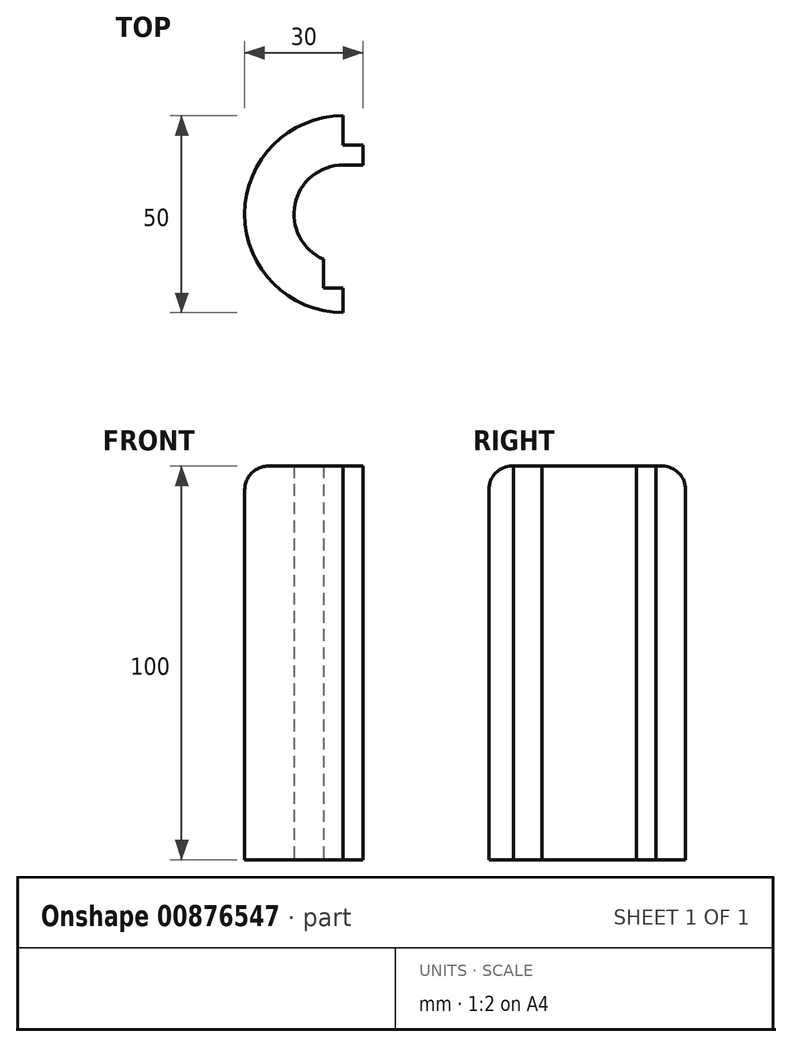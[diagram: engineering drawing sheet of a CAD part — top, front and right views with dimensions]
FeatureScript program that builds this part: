
annotation { "Feature Type Name" : "Feature", "Feature Type Description" : "" }
export const myFeature = defineFeature(function(context is Context, id is Id, definition is map)
    precondition{}
    {
        {
            var Q0;
            Q0=qCreatedBy(makeId("Top.planeOp"),FACE);
            var sketch = newSketch(context, id + "F0", { "sketchPlane" : qUnion([Q0])});
            skArc(sketch, "E0", {"start": v(0, 12.5) * mm, "mid": v(-12.24, 2.55) * mm, "end": v(-5, -11.46) * mm});
            skArc(sketch, "E1", {"start": v(0, 25) * mm, "mid": v(-25, 0) * mm, "end": v(0, -25) * mm});
            skLineSegment(sketch, "E2", {"start": v(0, -18.75) * mm, "end": v(0, -25) * mm});
            skLineSegment(sketch, "E3", {"start": v(0, 17.5) * mm, "end": v(0, 25) * mm});
            skLineSegment(sketch, "E4", {"start": v(0, 12.5) * mm, "end": v(5, 12.5) * mm});
            skLineSegment(sketch, "E5", {"start": v(5, 12.5) * mm, "end": v(5, 17.5) * mm});
            skLineSegment(sketch, "E6", {"start": v(5, 17.5) * mm, "end": v(0, 17.5) * mm});
            skLineSegment(sketch, "E7", {"start": v(0, -18.75) * mm, "end": v(-5, -18.75) * mm});
            skLineSegment(sketch, "E8", {"start": v(-5, -18.75) * mm, "end": v(-5, -11.46) * mm});
            skPoint(sketch, "E9.orphan", {"position": v(0, -12.5) * mm});
            skSolve(sketch);
        }
        {
            var Q0;
            Q0=makeQuery(id+"F0.imprint","IMPRINT",FACE,{"disambiguationData":[TD([[makeQuery(id+"F0.imprint","IMPRINT",EDGE,{"derivedFrom":sQuery(id+"F0.wireOp",EDGE,"E0")}),-1.0]])]});
            extrude(context, id + "F1", {"entities" : qUnion([Q0]), "depth" : 100 * mm, "offsetDistance" : 25 * mm});
        }
        {
            var Q0;
            Q0=makeQuery(id+"F1.opExtrude","CAP_EDGE",EDGE,{"disambiguationData":[OSD([sQuery(id+"F0.wireOp",EDGE,"E1")])],"isStart":false});
            fillet(context, id + "F2", {"entities" : qUnion([Q0]), "radius" : 6 * mm, "tangentPropagation" : true, "allowEdgeOverflow" : false});
        }
    });
